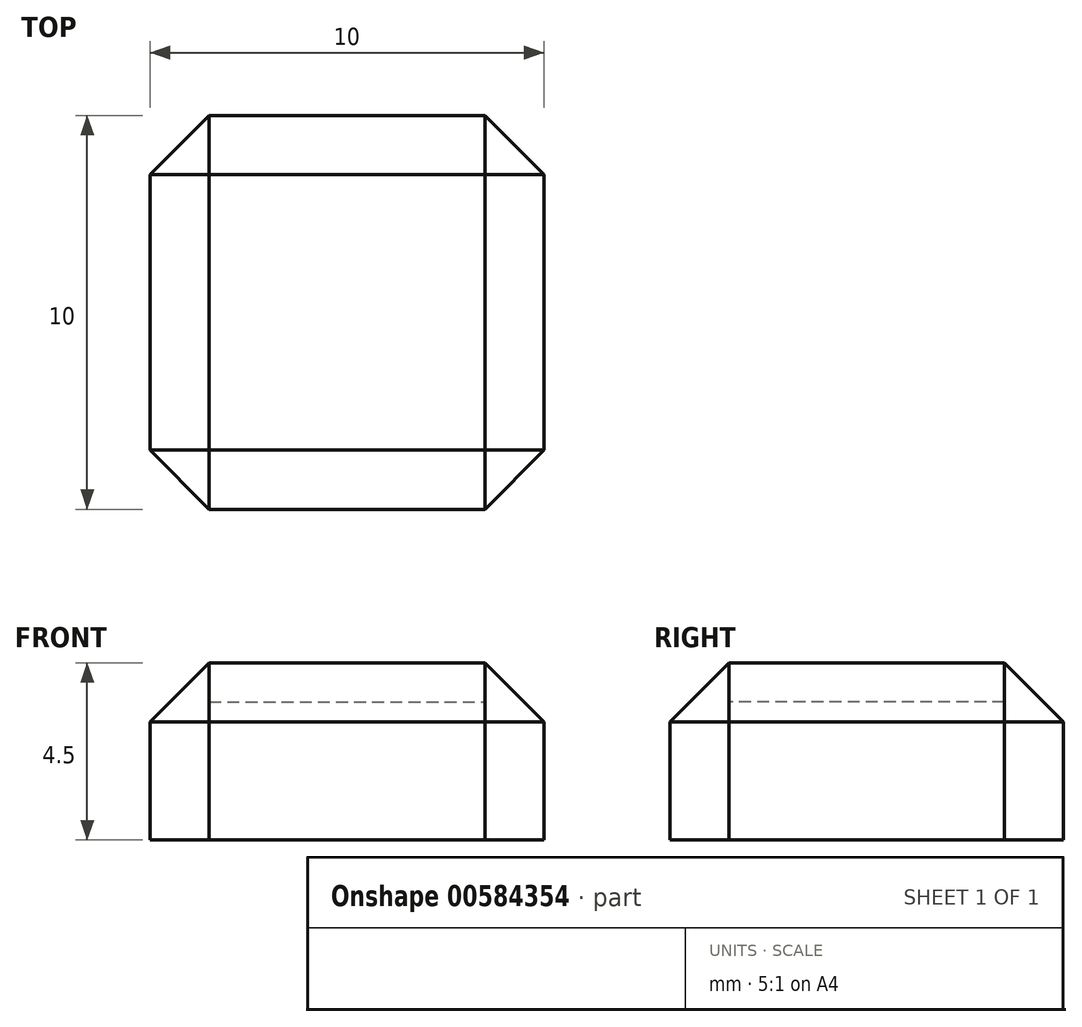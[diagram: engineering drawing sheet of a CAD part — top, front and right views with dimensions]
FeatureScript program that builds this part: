
annotation { "Feature Type Name" : "Feature", "Feature Type Description" : "" }
export const myFeature = defineFeature(function(context is Context, id is Id, definition is map)
    precondition{}
    {
        {
            var Q0;
            Q0=qCreatedBy(makeId("Top.planeOp"),FACE);
            var sketch = newSketch(context, id + "F0", { "sketchPlane" : qUnion([Q0])});
            skLineSegment(sketch, "E0.bottom", {"start": v(-3.5, 3.5) * mm, "end": v(3.5, 3.5) * mm});
            skLineSegment(sketch, "E0.top", {"start": v(-3.5, -3.5) * mm, "end": v(3.5, -3.5) * mm});
            skLineSegment(sketch, "E0.left", {"start": v(-3.5, 3.5) * mm, "end": v(-3.5, -3.5) * mm});
            skLineSegment(sketch, "E0.right", {"start": v(3.5, 3.5) * mm, "end": v(3.5, -3.5) * mm});
            skPoint(sketch, "E0.middle", {"position": v(0, 0) * mm});
            skLineSegment(sketch, "E1.bottom", {"start": v(-5, 5) * mm, "end": v(5, 5) * mm});
            skLineSegment(sketch, "E1.top", {"start": v(-5, -5) * mm, "end": v(5, -5) * mm});
            skLineSegment(sketch, "E1.left", {"start": v(-5, 5) * mm, "end": v(-5, -5) * mm});
            skLineSegment(sketch, "E1.right", {"start": v(5, 5) * mm, "end": v(5, -5) * mm});
            skSolve(sketch);
        }
        {
            var Q0;
            Q0=makeQuery(id+"F0.imprint","IMPRINT",FACE,{"disambiguationData":[TD([[makeQuery(id+"F0.imprint","IMPRINT",EDGE,{"derivedFrom":sQuery(id+"F0.wireOp",EDGE,"E0.bottom")}),1.0]])]});
            var Q1;
            Q1=makeQuery(id+"F0.imprint","IMPRINT",FACE,{"disambiguationData":[TD([[makeQuery(id+"F0.imprint","IMPRINT",EDGE,{"derivedFrom":sQuery(id+"F0.wireOp",EDGE,"E0.bottom")}),-1.0]])]});
            extrude(context, id + "F1", {"entities" : qUnion([Q0, Q1]), "depth" : 1 * mm, "offsetDistance" : 25 * mm});
        }
        {
            var Q0;
            Q0=makeQuery(id+"F0.imprint","IMPRINT",FACE,{"disambiguationData":[TD([[makeQuery(id+"F0.imprint","IMPRINT",EDGE,{"derivedFrom":sQuery(id+"F0.wireOp",EDGE,"E0.bottom")}),1.0]])]});
            extrude(context, id + "F2", {"entities" : qUnion([Q0]), "operationType" : NewBodyOperationType.ADD, "oppositeDirection" : true, "depth" : 3.5 * mm, "offsetDistance" : 25 * mm});
        }
        {
            var Q0;
            {var subQ0=sQuery(id+"F0.wireOp",EDGE,"E1.right");var subQ1=sQuery(id+"F0.wireOp",EDGE,"E1.top");Q0=makeQuery(id+"F2.boolean.opBoolean","MERGE",EDGE,{"derivedFrom":[makeQuery(id+"F1.opExtrude","SWEPT_EDGE",EDGE,{"disambiguationData":[OSD([subQ1,subQ0])]}),makeQuery(id+"F2.opExtrude","SWEPT_EDGE",EDGE,{"disambiguationData":[OSD([subQ1,subQ0])]})]});}
            var Q1;
            {var subQ0=sQuery(id+"F0.wireOp",EDGE,"E1.left");var subQ1=sQuery(id+"F0.wireOp",EDGE,"E1.top");Q1=makeQuery(id+"F2.boolean.opBoolean","MERGE",EDGE,{"derivedFrom":[makeQuery(id+"F1.opExtrude","SWEPT_EDGE",EDGE,{"disambiguationData":[OSD([subQ1,subQ0])]}),makeQuery(id+"F2.opExtrude","SWEPT_EDGE",EDGE,{"disambiguationData":[OSD([subQ1,subQ0])]})]});}
            var Q2;
            {var subQ0=sQuery(id+"F0.wireOp",EDGE,"E1.left");var subQ1=sQuery(id+"F0.wireOp",EDGE,"E1.bottom");Q2=makeQuery(id+"F2.boolean.opBoolean","MERGE",EDGE,{"derivedFrom":[makeQuery(id+"F1.opExtrude","SWEPT_EDGE",EDGE,{"disambiguationData":[OSD([subQ1,subQ0])]}),makeQuery(id+"F2.opExtrude","SWEPT_EDGE",EDGE,{"disambiguationData":[OSD([subQ1,subQ0])]})]});}
            var Q3;
            {var subQ0=sQuery(id+"F0.wireOp",EDGE,"E1.right");var subQ1=sQuery(id+"F0.wireOp",EDGE,"E1.bottom");Q3=makeQuery(id+"F2.boolean.opBoolean","MERGE",EDGE,{"derivedFrom":[makeQuery(id+"F1.opExtrude","SWEPT_EDGE",EDGE,{"disambiguationData":[OSD([subQ1,subQ0])]}),makeQuery(id+"F2.opExtrude","SWEPT_EDGE",EDGE,{"disambiguationData":[OSD([subQ1,subQ0])]})]});}
            var Q4;
            Q4=makeQuery(id+"F1.opExtrude","CAP_EDGE",EDGE,{"disambiguationData":[OSD([sQuery(id+"F0.wireOp",EDGE,"E1.top")])],"isStart":false});
            var Q5;
            Q5=makeQuery(id+"F1.opExtrude","CAP_EDGE",EDGE,{"disambiguationData":[OSD([sQuery(id+"F0.wireOp",EDGE,"E1.bottom")])],"isStart":false});
            var Q6;
            Q6=makeQuery(id+"F1.opExtrude","CAP_EDGE",EDGE,{"disambiguationData":[OSD([sQuery(id+"F0.wireOp",EDGE,"E1.left")])],"isStart":false});
            var Q7;
            Q7=makeQuery(id+"F1.opExtrude","CAP_EDGE",EDGE,{"disambiguationData":[OSD([sQuery(id+"F0.wireOp",EDGE,"E1.right")])],"isStart":false});
            chamfer(context, id + "F3", {"entities" : qUnion([Q0, Q1, Q2, Q3, Q4, Q5, Q6, Q7]), "width" : 1.5 * mm, "tangentPropagation" : true});
        }
    });
